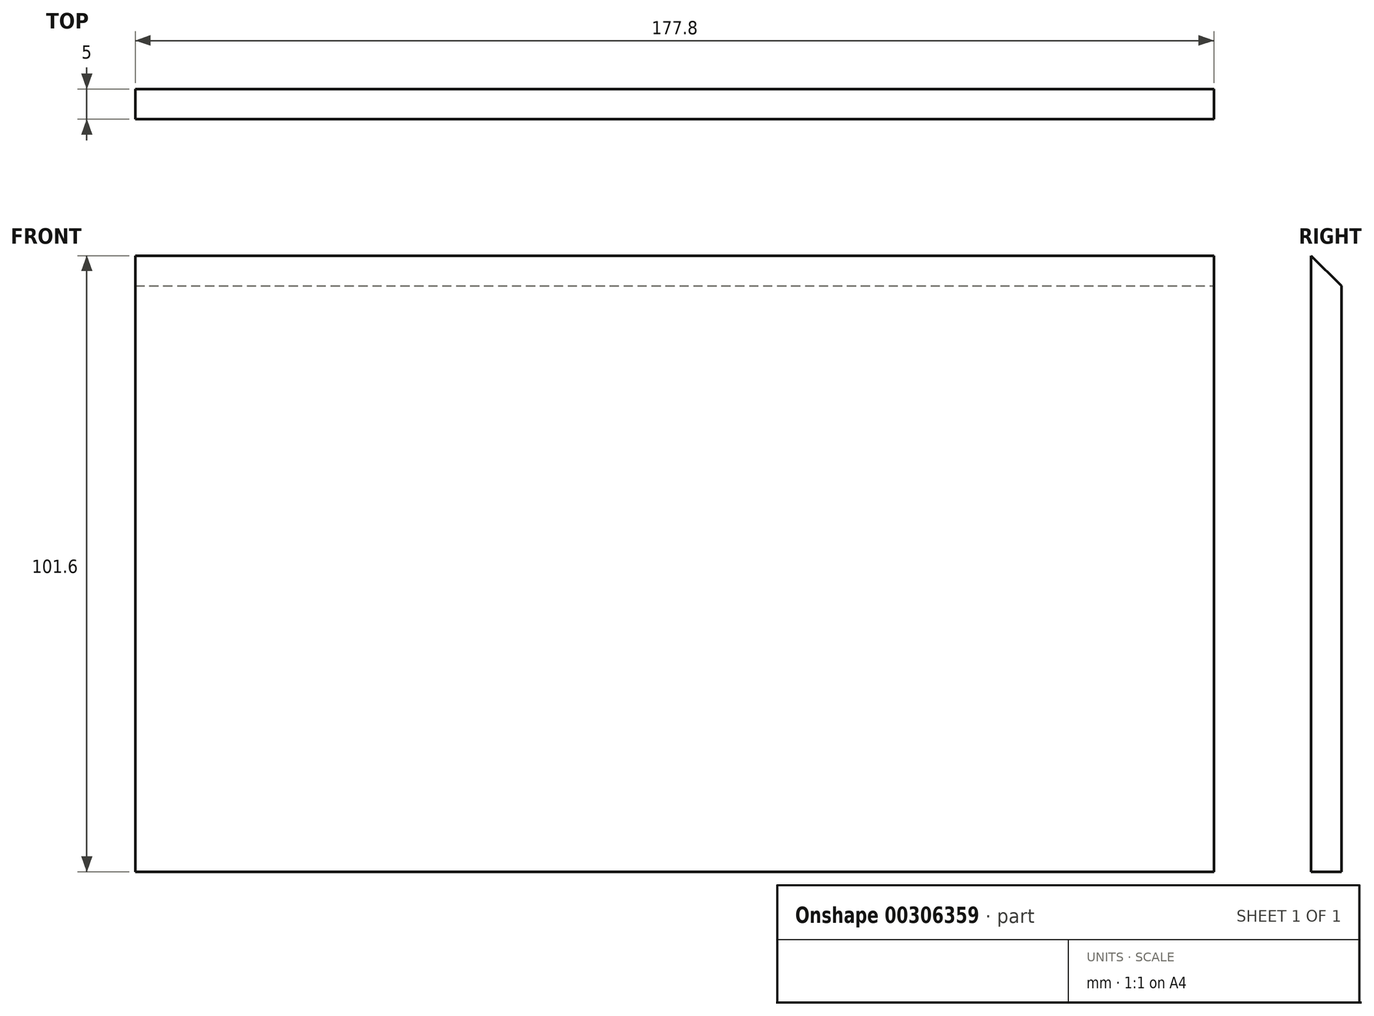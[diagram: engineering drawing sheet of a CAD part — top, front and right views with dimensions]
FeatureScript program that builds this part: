
annotation { "Feature Type Name" : "Feature", "Feature Type Description" : "" }
export const myFeature = defineFeature(function(context is Context, id is Id, definition is map)
    precondition{}
    {
        {
            var Q0;
            Q0=qCreatedBy(makeId("Front.planeOp"),FACE);
            var sketch = newSketch(context, id + "F0", { "sketchPlane" : qUnion([Q0])});
            skLineSegment(sketch, "E0.bottom", {"start": v(88.9, -50.8) * mm, "end": v(-88.9, -50.8) * mm});
            skLineSegment(sketch, "E0.top", {"start": v(88.9, 50.8) * mm, "end": v(-88.9, 50.8) * mm});
            skLineSegment(sketch, "E0.left", {"start": v(88.9, -50.8) * mm, "end": v(88.9, 50.8) * mm});
            skLineSegment(sketch, "E0.right", {"start": v(-88.9, -50.8) * mm, "end": v(-88.9, 50.8) * mm});
            skPoint(sketch, "E0.middle", {"position": v(0, 0) * mm});
            skSolve(sketch);
        }
        {
            var Q0;
            Q0 = qSketchRegion(id + "F0", true);
            extrude(context, id + "F1", {"entities" : qUnion([Q0]), "depth" : 5 * mm});
        }
        {
            var Q0;
            Q0=makeQuery(id+"F1.opExtrude","SWEPT_FACE",FACE,{"disambiguationData":[OSD([sQuery(id+"F0.wireOp",EDGE,"E0.left")])]});
            var sketch = newSketch(context, id + "F2", { "sketchPlane" : qUnion([Q0])});
            skLineSegment(sketch, "E1", {"start": v(-5, 50.8) * mm, "end": v(0, 45.8) * mm});
            skSolve(sketch);
        }
        {
            var Q0;
            {var subQ0=sQuery(id+"F2.wireOp",EDGE,"E1");Q0=makeQuery(id+"F2.imprint","IMPRINT",FACE,{"disambiguationData":[TD([[makeQuery(id+"F2.imprint","IMPRINT",EDGE,{"derivedFrom":subQ0}),1.0]])]});}
            extrude(context, id + "F3", {"entities" : qUnion([Q0]), "operationType" : NewBodyOperationType.REMOVE, "endBound" : BoundingType.THROUGH_ALL, "oppositeDirection" : true, "depth" : 25.4 * mm});
        }
    });
